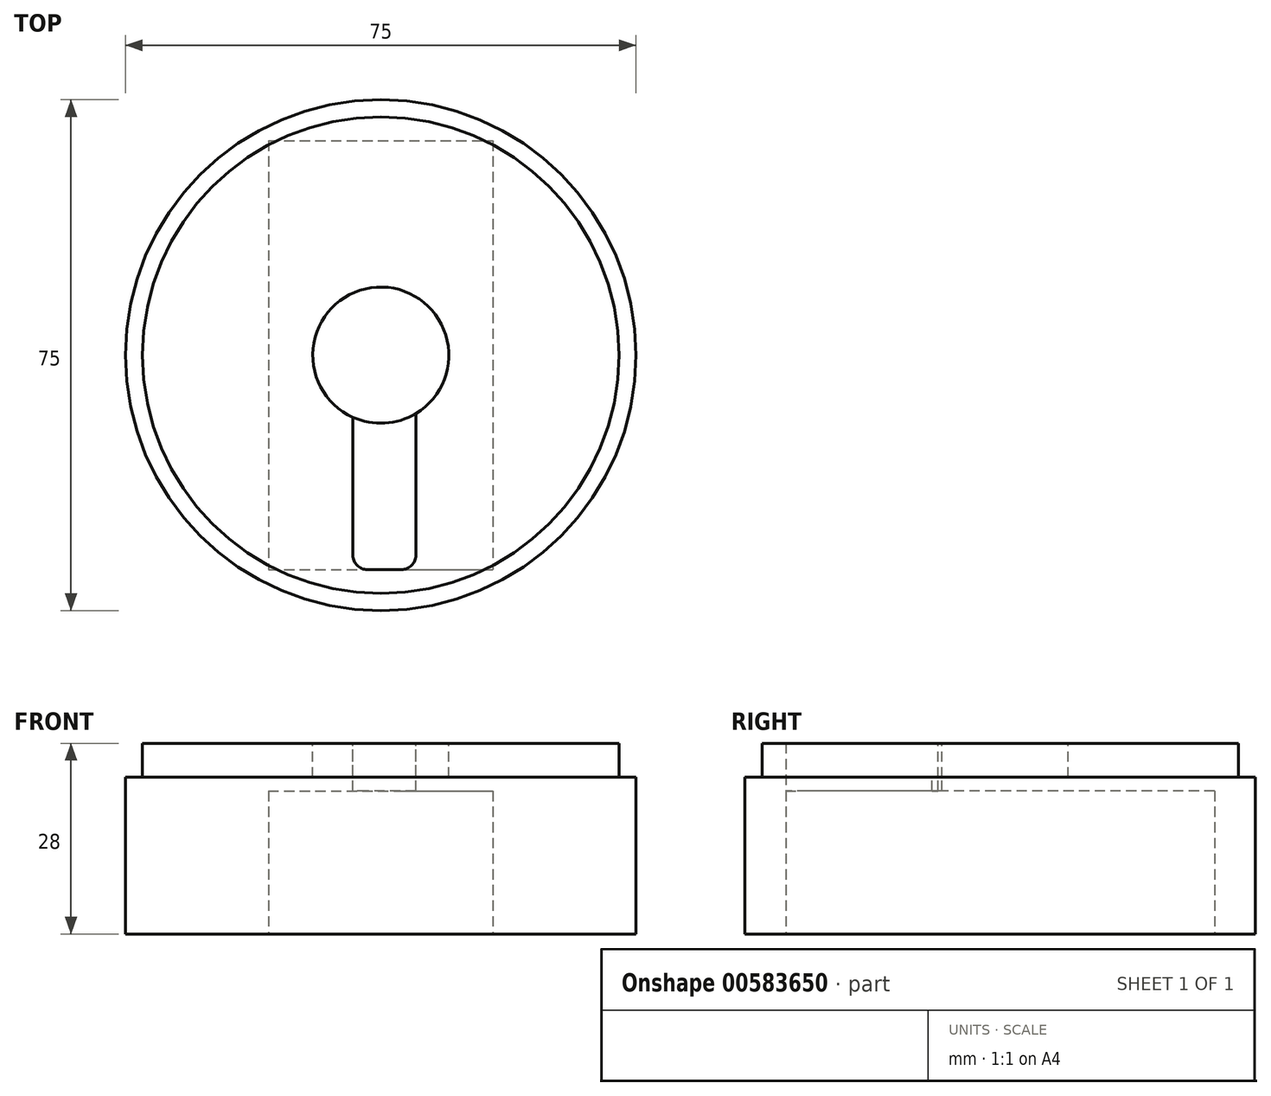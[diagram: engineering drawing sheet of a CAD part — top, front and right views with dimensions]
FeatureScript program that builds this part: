
annotation { "Feature Type Name" : "Feature", "Feature Type Description" : "" }
export const myFeature = defineFeature(function(context is Context, id is Id, definition is map)
    precondition{}
    {
        {
            var Q0;
            Q0=qCreatedBy(makeId("Top.planeOp"),FACE);
            var sketch = newSketch(context, id + "F0", { "sketchPlane" : qUnion([Q0])});
            skCircle(sketch, "E0", {"center": v(0, 0) * mm, "radius": 37.5 * mm});
            skSolve(sketch);
        }
        {
            var Q0;
            Q0=qSketchRegion(id+"F0",true);
            extrude(context, id + "F1", {"entities" : qUnion([Q0]), "depth" : 28 * mm, "offsetDistance" : 25 * mm});
        }
        {
            var Q0;
            Q0=makeQuery(id+"F1.opExtrude","CAP_FACE",FACE,{"disambiguationData":[OSD([sQuery(id+"F0.wireOp",EDGE,"E0")])],"isStart":true});
            var sketch = newSketch(context, id + "F2", { "sketchPlane" : qUnion([Q0])});
            skLineSegment(sketch, "E1.bottom", {"start": v(-16.5, -31.5) * mm, "end": v(16.5, -31.5) * mm});
            skLineSegment(sketch, "E1.top", {"start": v(-16.5, 31.5) * mm, "end": v(16.5, 31.5) * mm});
            skLineSegment(sketch, "E1.left", {"start": v(-16.5, -31.5) * mm, "end": v(-16.5, 31.5) * mm});
            skLineSegment(sketch, "E1.right", {"start": v(16.5, -31.5) * mm, "end": v(16.5, 31.5) * mm});
            skPoint(sketch, "E1.middle", {"position": v(0, 0) * mm});
            skSolve(sketch);
        }
        {
            var Q0;
            Q0=qSketchRegion(id+"F2",true);
            extrude(context, id + "F3", {"entities" : qUnion([Q0]), "operationType" : NewBodyOperationType.REMOVE, "oppositeDirection" : true, "depth" : 21 * mm, "offsetDistance" : 25 * mm});
        }
        {
            var Q0;
            Q0=makeQuery(id+"F1.opExtrude","CAP_FACE",FACE,{"disambiguationData":[OSD([sQuery(id+"F0.wireOp",EDGE,"E0")])],"isStart":false});
            var sketch = newSketch(context, id + "F4", { "sketchPlane" : qUnion([Q0])});
            skCircle(sketch, "E2", {"center": v(0, 0) * mm, "radius": 10 * mm});
            skSolve(sketch);
        }
        {
            var Q0;
            Q0=qSketchRegion(id+"F4",true);
            extrude(context, id + "F5", {"entities" : qUnion([Q0]), "operationType" : NewBodyOperationType.REMOVE, "oppositeDirection" : true, "depth" : 5 * mm, "offsetDistance" : 25 * mm});
        }
        {
            var Q0;
            Q0=makeQuery(id+"F3.boolean.opBoolean","COPY",FACE,{"derivedFrom":makeQuery(id+"F3.opExtrude","CAP_FACE",FACE,{"disambiguationData":[OSD([sQuery(id+"F2.wireOp",EDGE,"E1.bottom"),sQuery(id+"F2.wireOp",EDGE,"E1.top"),sQuery(id+"F2.wireOp",EDGE,"E1.left"),sQuery(id+"F2.wireOp",EDGE,"E1.right")])],"isStart":false})});
            var sketch = newSketch(context, id + "F6", { "sketchPlane" : qUnion([Q0])});
            skArc(sketch, "E3", {"start": v(-1.99, 31.5) * mm, "mid": v(-4.1, 29.39) * mm, "end": v(-1.99, 27.28) * mm});
            skArc(sketch, "E4", {"start": v(3.05, 27.28) * mm, "mid": v(5.16, 29.39) * mm, "end": v(3.05, 31.5) * mm});
            skLineSegment(sketch, "E5", {"start": v(3.05, 27.28) * mm, "end": v(-1.99, 27.28) * mm});
            skPoint(sketch, "E6.0", {"position": v(0, 31.5) * mm});
            skLineSegment(sketch, "E7.0", {"start": v(-16.5, 31.5) * mm, "end": v(16.5, 31.5) * mm});
            skSolve(sketch);
        }
        {
            var Q0;
            Q0=qSketchRegion(id+"F6",true);
            extrude(context, id + "F7", {"entities" : qUnion([Q0]), "operationType" : NewBodyOperationType.REMOVE, "oppositeDirection" : true, "depth" : 25 * mm, "offsetDistance" : 25 * mm});
        }
        {
            var Q0;
            Q0=makeQuery(id+"F1.opExtrude","CAP_FACE",FACE,{"disambiguationData":[OSD([sQuery(id+"F0.wireOp",EDGE,"E0")])],"isStart":false});
            var sketch = newSketch(context, id + "F8", { "sketchPlane" : qUnion([Q0])});
            skLineSegment(sketch, "E8", {"start": v(-4.1, -29.39) * mm, "end": v(-4.1, -9.12) * mm});
            skLineSegment(sketch, "E9", {"start": v(5.16, -29.39) * mm, "end": v(5.16, -8.57) * mm});
            skSolve(sketch);
        }
        {
            var Q0;
            Q0=qSketchRegion(id+"F8",true);
            var Q1;
            {var subQ3=sQuery(id+"F8.wireOp",EDGE,"E8");Q1=makeQuery(id+"F8.imprint","IMPRINT",FACE,{"disambiguationData":[TD([[makeQuery(id+"F8.imprint","IMPRINT",EDGE,{"derivedFrom":subQ3}),-1.0]])]});}
            extrude(context, id + "F9", {"entities" : qUnion([Q0, Q1]), "operationType" : NewBodyOperationType.REMOVE, "oppositeDirection" : true, "depth" : 15 * mm, "offsetDistance" : 25 * mm});
        }
        {
            var Q0;
            Q0=makeQuery(id+"F1.opExtrude","CAP_FACE",FACE,{"disambiguationData":[OSD([sQuery(id+"F0.wireOp",EDGE,"E0")])],"isStart":false});
            var sketch = newSketch(context, id + "F10", { "sketchPlane" : qUnion([Q0])});
            skCircle(sketch, "E10", {"center": v(0, 0) * mm, "radius": 35 * mm});
            skCircle(sketch, "E11.0", {"center": v(0, 0) * mm, "radius": 37.5 * mm});
            skSolve(sketch);
        }
        {
            var Q0;
            Q0=qSketchRegion(id+"F10",true);
            extrude(context, id + "F11", {"entities" : qUnion([Q0]), "operationType" : NewBodyOperationType.REMOVE, "oppositeDirection" : true, "depth" : 5 * mm, "offsetDistance" : 25 * mm});
        }
    });
